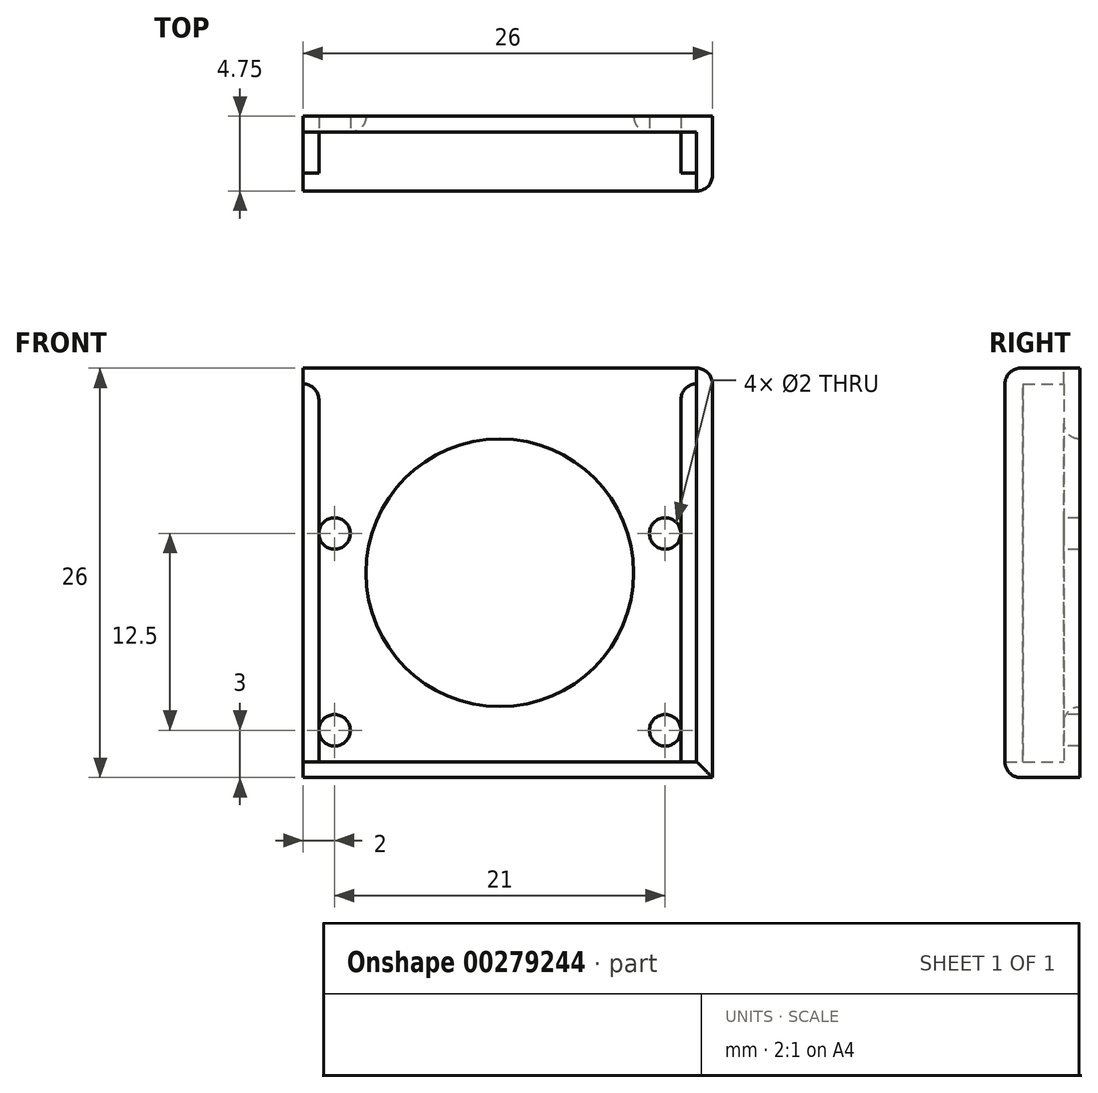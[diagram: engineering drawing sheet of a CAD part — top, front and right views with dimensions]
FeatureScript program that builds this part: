
annotation { "Feature Type Name" : "Feature", "Feature Type Description" : "" }
export const myFeature = defineFeature(function(context is Context, id is Id, definition is map)
    precondition{}
    {
        {
            var Q0;
            Q0=qCreatedBy(makeId("Front.planeOp"),FACE);
            var sketch = newSketch(context, id + "F0", { "sketchPlane" : qUnion([Q0])});
            skLineSegment(sketch, "E0.bottom", {"start": v(12.5, -12) * mm, "end": v(-12.5, -12) * mm});
            skLineSegment(sketch, "E0.top", {"start": v(12.5, 12) * mm, "end": v(-12.5, 12) * mm});
            skLineSegment(sketch, "E0.left", {"start": v(12.5, -12) * mm, "end": v(12.5, 12) * mm});
            skLineSegment(sketch, "E0.right", {"start": v(-12.5, -12) * mm, "end": v(-12.5, 12) * mm});
            skPoint(sketch, "E0.middle", {"position": v(0, 0) * mm});
            skCircle(sketch, "E1", {"center": v(-10.5, -10) * mm, "radius": 1 * mm});
            skCircle(sketch, "E2", {"center": v(-10.5, 2.5) * mm, "radius": 1 * mm});
            skCircle(sketch, "E3.MirrorC", {"center": v(10.5, 2.5) * mm, "radius": 1 * mm});
            skCircle(sketch, "E4.MirrorC", {"center": v(10.5, -10) * mm, "radius": 1 * mm});
            skLineSegment(sketch, "E5.bottom", {"start": v(13.5, -13) * mm, "end": v(-13.5, -13) * mm});
            skLineSegment(sketch, "E5.top", {"start": v(13.5, 13) * mm, "end": v(-13.5, 13) * mm});
            skLineSegment(sketch, "E5.left", {"start": v(13.5, -13) * mm, "end": v(13.5, 13) * mm});
            skLineSegment(sketch, "E5.right", {"start": v(-13.5, -13) * mm, "end": v(-13.5, 13) * mm});
            skLineSegment(sketch, "E6.bottom", {"start": v(-13.5, 13) * mm, "end": v(-11.5, 13) * mm});
            skLineSegment(sketch, "E6.top", {"start": v(-13.5, -13) * mm, "end": v(-11.5, -13) * mm});
            skLineSegment(sketch, "E6.left", {"start": v(-13.5, 13) * mm, "end": v(-13.5, -13) * mm});
            skLineSegment(sketch, "E6.right", {"start": v(-11.5, 13) * mm, "end": v(-11.5, -13) * mm});
            skLineSegment(sketch, "E7.MirrorCS", {"start": v(11.5, 13) * mm, "end": v(11.5, -13) * mm});
            skLineSegment(sketch, "E8", {"start": v(-12.5, 13) * mm, "end": v(-12.5, -13) * mm});
            skLineSegment(sketch, "E9.MirrorCS", {"start": v(12.5, 13) * mm, "end": v(12.5, -13) * mm});
            skCircle(sketch, "E10", {"center": v(0, 0) * mm, "radius": 8.5 * mm});
            skSolve(sketch);
        }
        {
            var Q0;
            {var subQ0=sQuery(id+"F0.wireOp",EDGE,"E6.left");Q0=makeQuery(id+"F0.imprint","IMPRINT",FACE,{"disambiguationData":[TD([[makeQuery(id+"F0.imprint","IMPRINT",EDGE,{"derivedFrom":subQ0}),1.0]])]});}
            var Q1;
            {var subQ0=sQuery(id+"F0.wireOp",EDGE,"E5.left");Q1=makeQuery(id+"F0.imprint","IMPRINT",FACE,{"disambiguationData":[TD([[makeQuery(id+"F0.imprint","IMPRINT",EDGE,{"derivedFrom":subQ0}),1.0]])]});}
            var Q2;
            {var subQ0=sQuery(id+"F0.wireOp",EDGE,"E7.MirrorCS");var subQ1=sQuery(id+"F0.wireOp",EDGE,"E0.bottom");var subQ2=makeQuery(id+"F0.imprint","INTERSECT",VERTEX,{"derivedFrom":[subQ1,subQ0]});Q2=makeQuery(id+"F0.imprint","IMPRINT",FACE,{"disambiguationData":[TD([[makeQuery(id+"F0.imprint","IMPRINT",EDGE,{"disambiguationData":[TD([[subQ2,-1.0]])],"derivedFrom":subQ1}),1.0]])]});}
            var Q3;
            {var subQ0=sQuery(id+"F0.wireOp",EDGE,"E8");var subQ1=sQuery(id+"F0.wireOp",EDGE,"E0.bottom");var subQ2=makeQuery(id+"F0.imprint","INTERSECT",VERTEX,{"derivedFrom":[subQ1,subQ0]});Q3=makeQuery(id+"F0.imprint","IMPRINT",FACE,{"disambiguationData":[TD([[makeQuery(id+"F0.imprint","IMPRINT",EDGE,{"disambiguationData":[TD([[subQ2,1.0]])],"derivedFrom":subQ1}),1.0]])]});}
            var Q4;
            {var subQ0=sQuery(id+"F0.wireOp",EDGE,"E9.MirrorCS");var subQ1=sQuery(id+"F0.wireOp",EDGE,"E0.bottom");var subQ2=makeQuery(id+"F0.imprint","INTERSECT",VERTEX,{"derivedFrom":[subQ1,subQ0]});Q4=makeQuery(id+"F0.imprint","IMPRINT",FACE,{"disambiguationData":[TD([[makeQuery(id+"F0.imprint","IMPRINT",EDGE,{"disambiguationData":[TD([[subQ2,-1.0]])],"derivedFrom":subQ1}),1.0]])]});}
            extrude(context, id + "F1", {"entities" : qUnion([Q0, Q1, Q2, Q3, Q4]), "depth" : 3.75 * mm});
        }
        {
            var Q0;
            {var subQ3=sQuery(id+"F0.wireOp",EDGE,"E8");var subQ4=sQuery(id+"F0.wireOp",EDGE,"E0.bottom");var subQ5=makeQuery(id+"F0.imprint","INTERSECT",VERTEX,{"derivedFrom":[subQ4,subQ3]});Q0=makeQuery(id+"F0.imprint","IMPRINT",FACE,{"disambiguationData":[TD([[makeQuery(id+"F0.imprint","IMPRINT",EDGE,{"disambiguationData":[TD([[subQ5,1.0]])],"derivedFrom":subQ4}),-1.0]])]});}
            var Q1;
            {var subQ5=sQuery(id+"F0.wireOp",EDGE,"E9.MirrorCS");var subQ7=sQuery(id+"F0.wireOp",EDGE,"E0.bottom");var subQ8=makeQuery(id+"F0.imprint","INTERSECT",VERTEX,{"derivedFrom":[subQ7,subQ5]});Q1=makeQuery(id+"F0.imprint","IMPRINT",FACE,{"disambiguationData":[TD([[makeQuery(id+"F0.imprint","IMPRINT",EDGE,{"disambiguationData":[TD([[subQ8,-1.0]])],"derivedFrom":subQ7}),-1.0]])]});}
            extrude(context, id + "F2", {"entities" : qUnion([Q0, Q1]), "operationType" : NewBodyOperationType.ADD, "depth" : 2.6 * mm});
        }
        {
            var Q0;
            {var subQ1=sQuery(id+"F0.wireOp",EDGE,"E1");Q0=makeQuery(id+"F0.imprint","IMPRINT",FACE,{"disambiguationData":[TD([[makeQuery(id+"F0.imprint","IMPRINT",EDGE,{"derivedFrom":subQ1}),-1.0]])]});}
            var Q1;
            {var subQ0=sQuery(id+"F0.wireOp",EDGE,"E7.MirrorCS");var subQ1=sQuery(id+"F0.wireOp",EDGE,"E0.top");var subQ2=makeQuery(id+"F0.imprint","INTERSECT",VERTEX,{"derivedFrom":[subQ1,subQ0]});Q1=makeQuery(id+"F0.imprint","IMPRINT",FACE,{"disambiguationData":[TD([[makeQuery(id+"F0.imprint","IMPRINT",EDGE,{"disambiguationData":[TD([[subQ2,-1.0]])],"derivedFrom":subQ1}),-1.0]])]});}
            var Q2;
            {var subQ0=sQuery(id+"F0.wireOp",EDGE,"E6.left");Q2=makeQuery(id+"F0.imprint","IMPRINT",FACE,{"disambiguationData":[TD([[makeQuery(id+"F0.imprint","IMPRINT",EDGE,{"derivedFrom":subQ0}),1.0]])]});}
            var Q3;
            {var subQ3=sQuery(id+"F0.wireOp",EDGE,"E8");var subQ4=sQuery(id+"F0.wireOp",EDGE,"E0.bottom");var subQ5=makeQuery(id+"F0.imprint","INTERSECT",VERTEX,{"derivedFrom":[subQ4,subQ3]});Q3=makeQuery(id+"F0.imprint","IMPRINT",FACE,{"disambiguationData":[TD([[makeQuery(id+"F0.imprint","IMPRINT",EDGE,{"disambiguationData":[TD([[subQ5,1.0]])],"derivedFrom":subQ4}),-1.0]])]});}
            var Q4;
            {var subQ0=sQuery(id+"F0.wireOp",EDGE,"E8");var subQ1=sQuery(id+"F0.wireOp",EDGE,"E0.top");var subQ2=makeQuery(id+"F0.imprint","INTERSECT",VERTEX,{"derivedFrom":[subQ1,subQ0]});Q4=makeQuery(id+"F0.imprint","IMPRINT",FACE,{"disambiguationData":[TD([[makeQuery(id+"F0.imprint","IMPRINT",EDGE,{"disambiguationData":[TD([[subQ2,1.0]])],"derivedFrom":subQ1}),-1.0]])]});}
            var Q5;
            {var subQ0=sQuery(id+"F0.wireOp",EDGE,"E8");var subQ1=sQuery(id+"F0.wireOp",EDGE,"E0.bottom");var subQ2=makeQuery(id+"F0.imprint","INTERSECT",VERTEX,{"derivedFrom":[subQ1,subQ0]});Q5=makeQuery(id+"F0.imprint","IMPRINT",FACE,{"disambiguationData":[TD([[makeQuery(id+"F0.imprint","IMPRINT",EDGE,{"disambiguationData":[TD([[subQ2,1.0]])],"derivedFrom":subQ1}),1.0]])]});}
            var Q6;
            {var subQ0=sQuery(id+"F0.wireOp",EDGE,"E7.MirrorCS");var subQ1=sQuery(id+"F0.wireOp",EDGE,"E0.bottom");var subQ2=makeQuery(id+"F0.imprint","INTERSECT",VERTEX,{"derivedFrom":[subQ1,subQ0]});Q6=makeQuery(id+"F0.imprint","IMPRINT",FACE,{"disambiguationData":[TD([[makeQuery(id+"F0.imprint","IMPRINT",EDGE,{"disambiguationData":[TD([[subQ2,-1.0]])],"derivedFrom":subQ1}),1.0]])]});}
            var Q7;
            {var subQ0=sQuery(id+"F0.wireOp",EDGE,"E9.MirrorCS");var subQ1=sQuery(id+"F0.wireOp",EDGE,"E0.bottom");var subQ2=makeQuery(id+"F0.imprint","INTERSECT",VERTEX,{"derivedFrom":[subQ1,subQ0]});Q7=makeQuery(id+"F0.imprint","IMPRINT",FACE,{"disambiguationData":[TD([[makeQuery(id+"F0.imprint","IMPRINT",EDGE,{"disambiguationData":[TD([[subQ2,-1.0]])],"derivedFrom":subQ1}),1.0]])]});}
            var Q8;
            {var subQ5=sQuery(id+"F0.wireOp",EDGE,"E9.MirrorCS");var subQ7=sQuery(id+"F0.wireOp",EDGE,"E0.bottom");var subQ8=makeQuery(id+"F0.imprint","INTERSECT",VERTEX,{"derivedFrom":[subQ7,subQ5]});Q8=makeQuery(id+"F0.imprint","IMPRINT",FACE,{"disambiguationData":[TD([[makeQuery(id+"F0.imprint","IMPRINT",EDGE,{"disambiguationData":[TD([[subQ8,-1.0]])],"derivedFrom":subQ7}),-1.0]])]});}
            var Q9;
            {var subQ0=sQuery(id+"F0.wireOp",EDGE,"E5.left");Q9=makeQuery(id+"F0.imprint","IMPRINT",FACE,{"disambiguationData":[TD([[makeQuery(id+"F0.imprint","IMPRINT",EDGE,{"derivedFrom":subQ0}),1.0]])]});}
            var Q10;
            {var subQ0=sQuery(id+"F0.wireOp",EDGE,"E9.MirrorCS");var subQ1=sQuery(id+"F0.wireOp",EDGE,"E0.top");var subQ2=makeQuery(id+"F0.imprint","INTERSECT",VERTEX,{"derivedFrom":[subQ1,subQ0]});Q10=makeQuery(id+"F0.imprint","IMPRINT",FACE,{"disambiguationData":[TD([[makeQuery(id+"F0.imprint","IMPRINT",EDGE,{"disambiguationData":[TD([[subQ2,-1.0]])],"derivedFrom":subQ1}),-1.0]])]});}
            extrude(context, id + "F3", {"entities" : qUnion([Q0, Q1, Q2, Q3, Q4, Q5, Q6, Q7, Q8, Q9, Q10]), "operationType" : NewBodyOperationType.ADD, "oppositeDirection" : true, "depth" : 1 * mm});
        }
        {
            var Q0;
            Q0=makeQuery(id+"F1.opExtrude","CAP_EDGE",EDGE,{"disambiguationData":[OSD([sQuery(id+"F0.wireOp",EDGE,"E6.left")])],"isStart":false});
            var Q1;
            Q1=makeQuery(id+"F1.opExtrude","CAP_EDGE",EDGE,{"disambiguationData":[OSD([sQuery(id+"F0.wireOp",EDGE,"E5.left")])],"isStart":false});
            var Q2;
            Q2=makeQuery(id+"F1.opExtrude","CAP_EDGE",EDGE,{"disambiguationData":[OSD([sQuery(id+"F0.wireOp",EDGE,"E5.bottom"),sQuery(id+"F0.wireOp",EDGE,"E6.top")])],"isStart":false});
            var Q3;
            {var subQ0=sQuery(id+"F0.wireOp",EDGE,"E6.left");var subQ1=sQuery(id+"F0.wireOp",EDGE,"E6.bottom");Q3=makeQuery(id+"F3.boolean.opBoolean","MERGE",EDGE,{"derivedFrom":[makeQuery(id+"F1.opExtrude","SWEPT_EDGE",EDGE,{"disambiguationData":[OSD([subQ1,subQ0])]}),makeQuery(id+"F3.opExtrude","SWEPT_EDGE",EDGE,{"disambiguationData":[OSD([subQ1,subQ0])]})]});}
            var Q4;
            {var subQ0=sQuery(id+"F0.wireOp",EDGE,"E5.left");var subQ1=sQuery(id+"F0.wireOp",EDGE,"E5.top");Q4=makeQuery(id+"F3.boolean.opBoolean","MERGE",EDGE,{"derivedFrom":[makeQuery(id+"F1.opExtrude","SWEPT_EDGE",EDGE,{"disambiguationData":[OSD([subQ1,subQ0])]}),makeQuery(id+"F3.opExtrude","SWEPT_EDGE",EDGE,{"disambiguationData":[OSD([subQ1,subQ0])]})]});}
            var Q5;
            Q5=makeQuery(id+"F1.opExtrude","CAP_EDGE",EDGE,{"disambiguationData":[OSD([sQuery(id+"F0.wireOp",EDGE,"E5.top")])],"isStart":false});
            var Q6;
            Q6=makeQuery(id+"F1.opExtrude","CAP_EDGE",EDGE,{"disambiguationData":[OSD([sQuery(id+"F0.wireOp",EDGE,"E6.bottom")])],"isStart":false});
            var Q7;
            Q7=makeQuery(id+"F2.opExtrude","SWEPT_EDGE",EDGE,{"disambiguationData":[OSD([sQuery(id+"F0.wireOp",EDGE,"E0.top"),sQuery(id+"F0.wireOp",EDGE,"E7.MirrorCS")])]});
            var Q8;
            Q8=makeQuery(id+"F2.opExtrude","SWEPT_EDGE",EDGE,{"disambiguationData":[OSD([sQuery(id+"F0.wireOp",EDGE,"E0.top"),sQuery(id+"F0.wireOp",EDGE,"E6.right")])]});
            var Q9;
            Q9=makeQuery(id+"F3.opExtrude","CAP_EDGE",EDGE,{"disambiguationData":[OSD([sQuery(id+"F0.wireOp",EDGE,"E10")])],"isStart":true});
            fillet(context, id + "F4", {"entities" : qUnion([Q0, Q1, Q2, Q3, Q4, Q5, Q6, Q7, Q8, Q9]), "radius" : 1 * mm, "tangentPropagation" : true, "allowEdgeOverflow" : false});
        }
    });
